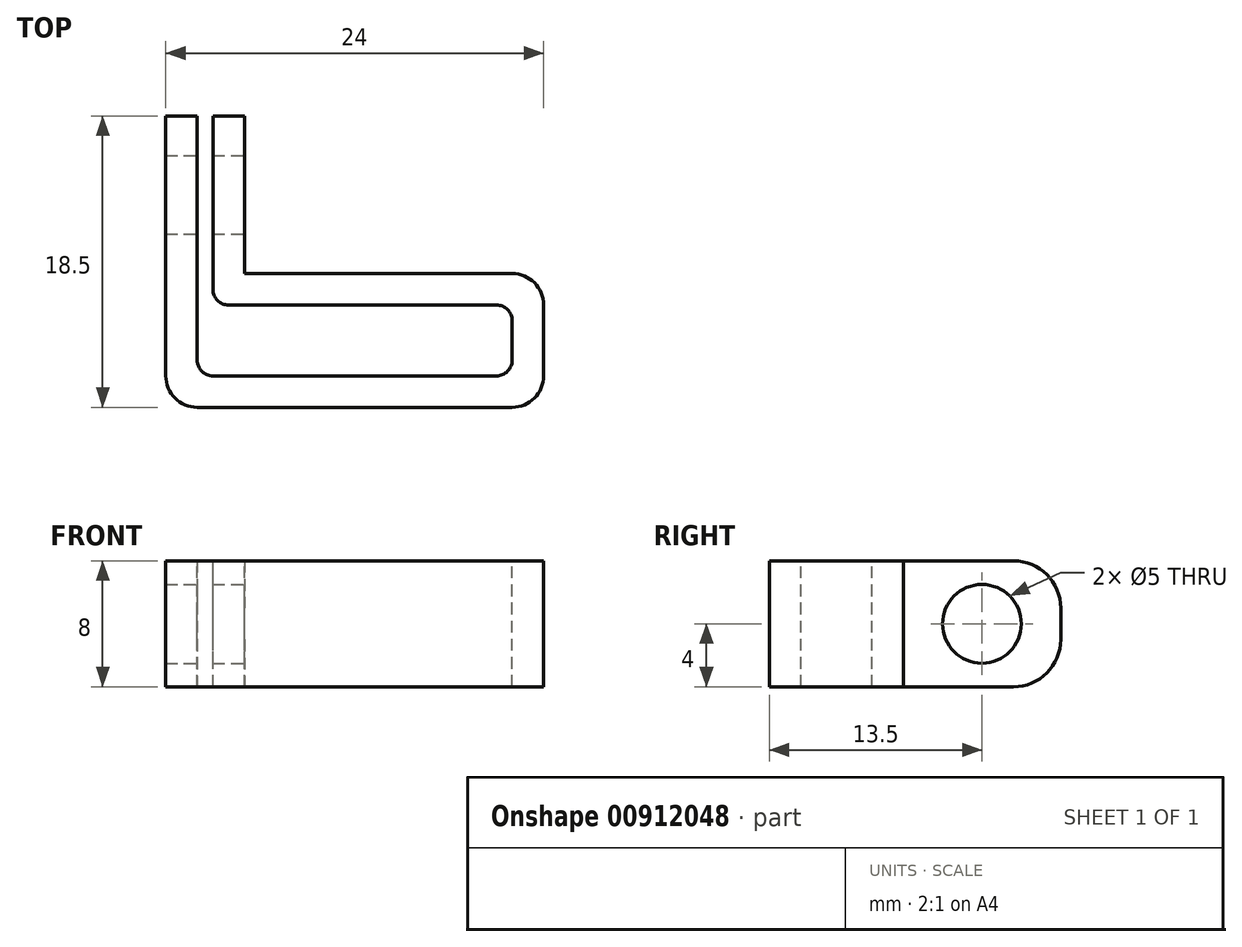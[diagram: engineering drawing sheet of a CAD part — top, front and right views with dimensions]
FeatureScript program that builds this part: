
annotation { "Feature Type Name" : "Feature", "Feature Type Description" : "" }
export const myFeature = defineFeature(function(context is Context, id is Id, definition is map)
    precondition{}
    {
        {
            var Q0;
            Q0=qCreatedBy(makeId("Top.planeOp"),FACE);
            var sketch = newSketch(context, id + "F0", { "sketchPlane" : qUnion([Q0])});
            skLineSegment(sketch, "E0", {"start": v(0, 16.5) * mm, "end": v(0, 0) * mm});
            skLineSegment(sketch, "E1", {"start": v(0, 0) * mm, "end": v(20, 0) * mm});
            skLineSegment(sketch, "E2", {"start": v(20, 0) * mm, "end": v(20, 4.5) * mm});
            skLineSegment(sketch, "E3", {"start": v(20, 4.5) * mm, "end": v(1, 4.5) * mm});
            skLineSegment(sketch, "E4", {"start": v(1, 4.5) * mm, "end": v(1, 16.5) * mm});
            skLineSegment(sketch, "E5", {"start": v(3, 6.5) * mm, "end": v(22, 6.5) * mm});
            skLineSegment(sketch, "E6", {"start": v(22, 6.5) * mm, "end": v(22, -2) * mm});
            skLineSegment(sketch, "E7", {"start": v(22, -2) * mm, "end": v(-2, -2) * mm});
            skLineSegment(sketch, "E8", {"start": v(-2, -2) * mm, "end": v(-2, 16.5) * mm});
            skLineSegment(sketch, "E9", {"start": v(-2, 16.5) * mm, "end": v(0, 16.5) * mm});
            skLineSegment(sketch, "E10", {"start": v(3, 16.5) * mm, "end": v(3, 6.5) * mm});
            skLineSegment(sketch, "E11", {"start": v(1, 16.5) * mm, "end": v(3, 16.5) * mm});
            skSolve(sketch);
        }
        {
            var Q0;
            Q0=qSketchRegion(id+"F0",true);
            extrude(context, id + "F1", {"entities" : qUnion([Q0]), "oppositeDirection" : true, "depth" : 8 * mm, "offsetDistance" : 25 * mm});
        }
        {
            var Q0;
            Q0=makeQuery(id+"F1.opExtrude","SWEPT_FACE",FACE,{"disambiguationData":[OSD([sQuery(id+"F0.wireOp",EDGE,"E10")])]});
            var sketch = newSketch(context, id + "F2", { "sketchPlane" : qUnion([Q0])});
            skCircle(sketch, "E12", {"center": v(11.5, -4) * mm, "radius": 2.5 * mm});
            skSolve(sketch);
        }
        {
            var Q0;
            Q0=makeQuery(id+"F1.opExtrude","CAP_EDGE",EDGE,{"disambiguationData":[OSD([sQuery(id+"F0.wireOp",EDGE,"guWewKpP-GbmB-BwNR-hQwf-DG9Nlq2iEjPg"),sQuery(id+"F0.wireOp",EDGE,"jrIloHjD-4TYg-XnnB-sxLV-LR2xORgdilK4")])],"isStart":true});
            var Q1;
            Q1=makeQuery(id+"F1.opExtrude","CAP_EDGE",EDGE,{"disambiguationData":[OSD([sQuery(id+"F0.wireOp",EDGE,"E9")])],"isStart":true});
            var Q2;
            Q2=makeQuery(id+"F1.opExtrude","CAP_EDGE",EDGE,{"disambiguationData":[OSD([sQuery(id+"F0.wireOp",EDGE,"E9")])],"isStart":false});
            var Q3;
            Q3=makeQuery(id+"F1.opExtrude","CAP_EDGE",EDGE,{"disambiguationData":[OSD([sQuery(id+"F0.wireOp",EDGE,"guWewKpP-GbmB-BwNR-hQwf-DG9Nlq2iEjPg"),sQuery(id+"F0.wireOp",EDGE,"jrIloHjD-4TYg-XnnB-sxLV-LR2xORgdilK4")])],"isStart":false});
            var Q4;
            Q4=makeQuery(id+"F1.opExtrude","CAP_EDGE",EDGE,{"disambiguationData":[OSD([sQuery(id+"F0.wireOp",EDGE,"E11")])],"isStart":true});
            var Q5;
            Q5=makeQuery(id+"F1.opExtrude","CAP_EDGE",EDGE,{"disambiguationData":[OSD([sQuery(id+"F0.wireOp",EDGE,"E11")])],"isStart":false});
            fillet(context, id + "F3", {"entities" : qUnion([Q0, Q1, Q2, Q3, Q4, Q5]), "radius" : 3 * mm, "tangentPropagation" : true, "allowEdgeOverflow" : false});
        }
        {
            var Q0;
            Q0=makeQuery(id+"F2.imprint","IMPRINT",FACE,{"disambiguationData":[TD([[makeQuery(id+"F2.imprint","IMPRINT",EDGE,{"derivedFrom":sQuery(id+"F2.wireOp",EDGE,"E12")}),1.0]])]});
            extrude(context, id + "F4", {"entities" : qUnion([Q0]), "operationType" : NewBodyOperationType.REMOVE, "endBound" : BoundingType.THROUGH_ALL, "oppositeDirection" : true, "depth" : 25 * mm, "offsetDistance" : 25 * mm});
        }
        {
            var Q0;
            Q0=makeQuery(id+"F1.opExtrude","SWEPT_EDGE",EDGE,{"disambiguationData":[OSD([sQuery(id+"F0.wireOp",EDGE,"E5"),sQuery(id+"F0.wireOp",EDGE,"E6")])]});
            var Q1;
            Q1=makeQuery(id+"F1.opExtrude","SWEPT_EDGE",EDGE,{"disambiguationData":[OSD([sQuery(id+"F0.wireOp",EDGE,"E6"),sQuery(id+"F0.wireOp",EDGE,"E7")])]});
            var Q2;
            Q2=makeQuery(id+"F1.opExtrude","SWEPT_EDGE",EDGE,{"disambiguationData":[OSD([sQuery(id+"F0.wireOp",EDGE,"E7"),sQuery(id+"F0.wireOp",EDGE,"E8")])]});
            fillet(context, id + "F5", {"entities" : qUnion([Q0, Q1, Q2]), "radius" : 2 * mm, "tangentPropagation" : true, "allowEdgeOverflow" : false});
        }
        {
            var Q0;
            Q0=makeQuery(id+"F1.opExtrude","SWEPT_EDGE",EDGE,{"disambiguationData":[OSD([sQuery(id+"F0.wireOp",EDGE,"E2"),sQuery(id+"F0.wireOp",EDGE,"E3")])]});
            var Q1;
            Q1=makeQuery(id+"F1.opExtrude","SWEPT_EDGE",EDGE,{"disambiguationData":[OSD([sQuery(id+"F0.wireOp",EDGE,"E1"),sQuery(id+"F0.wireOp",EDGE,"E2")])]});
            var Q2;
            Q2=makeQuery(id+"F1.opExtrude","SWEPT_EDGE",EDGE,{"disambiguationData":[OSD([sQuery(id+"F0.wireOp",EDGE,"E0"),sQuery(id+"F0.wireOp",EDGE,"E1")])]});
            var Q3;
            Q3=makeQuery(id+"F1.opExtrude","SWEPT_EDGE",EDGE,{"disambiguationData":[OSD([sQuery(id+"F0.wireOp",EDGE,"E3"),sQuery(id+"F0.wireOp",EDGE,"E4")])]});
            fillet(context, id + "F6", {"entities" : qUnion([Q0, Q1, Q2, Q3]), "radius" : 1 * mm, "tangentPropagation" : true, "allowEdgeOverflow" : false});
        }
    });
